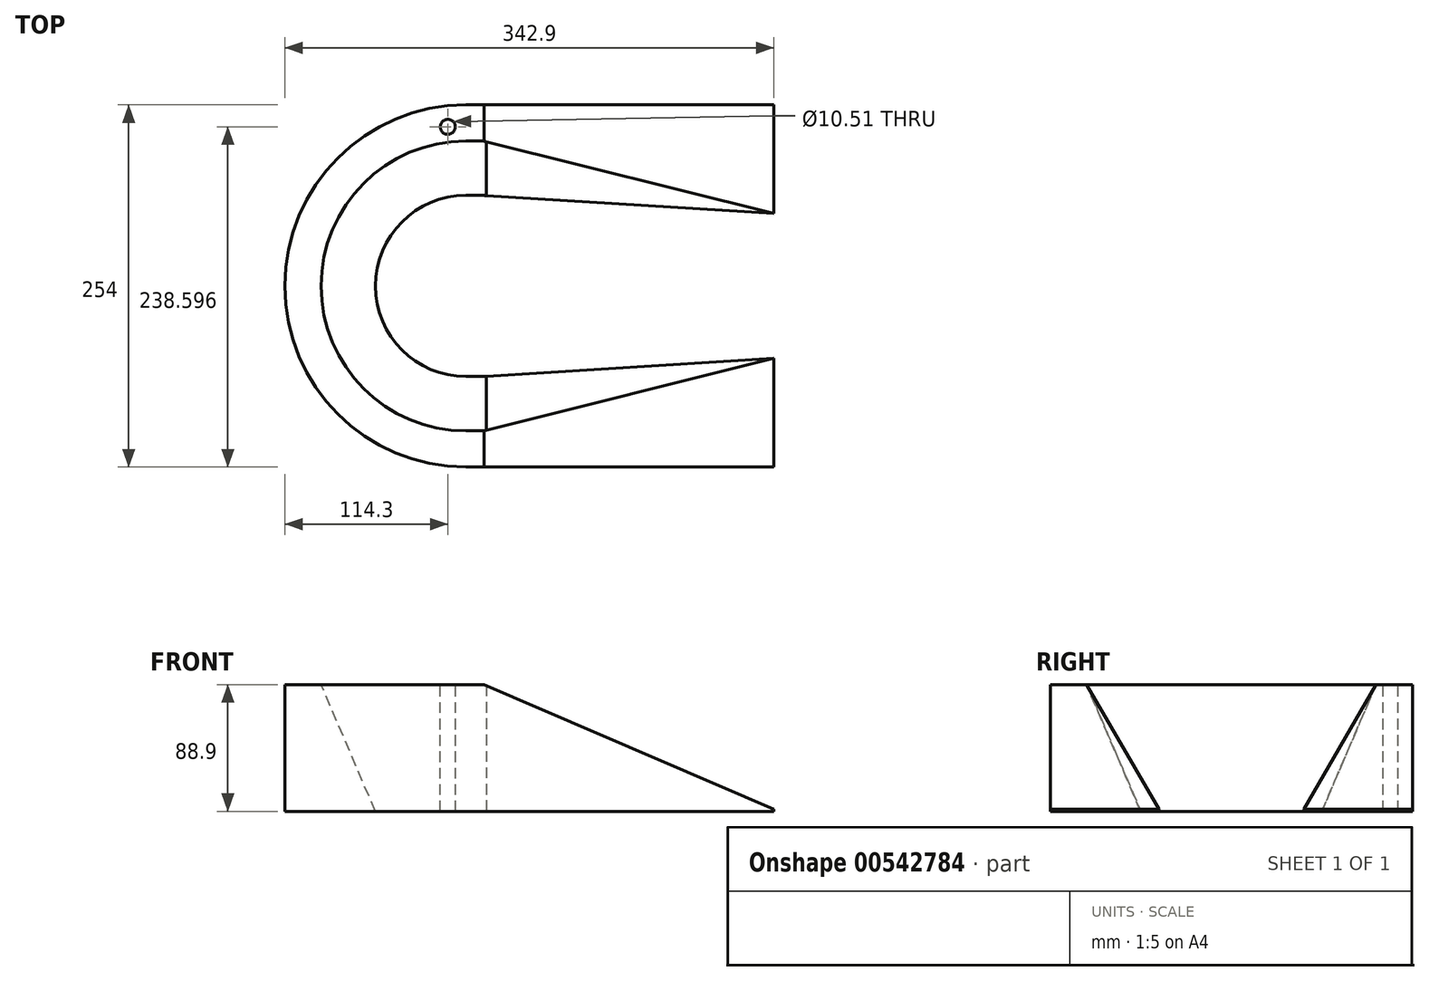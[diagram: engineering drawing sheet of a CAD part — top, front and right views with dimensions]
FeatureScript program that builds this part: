
annotation { "Feature Type Name" : "Feature", "Feature Type Description" : "" }
export const myFeature = defineFeature(function(context is Context, id is Id, definition is map)
    precondition{}
    {
        {
            var Q0;
            Q0=qCreatedBy(makeId("Top.planeOp"),FACE);
            var sketch = newSketch(context, id + "F0", { "sketchPlane" : qUnion([Q0])});
            skArc(sketch, "E0", {"start": v(0, 101.6) * mm, "mid": v(-71.84, 71.84) * mm, "end": v(-101.6, 0) * mm});
            skLineSegment(sketch, "E1", {"start": v(0, 101.6) * mm, "end": v(12.7, 101.6) * mm});
            skLineSegment(sketch, "E2", {"start": v(0, 0) * mm, "end": v(-101.6, 0) * mm, "construction": true});
            skSolve(sketch);
        }
        {
            var Q0;
            Q0=qCreatedBy(makeId("Right.planeOp"),FACE);
            var Q1;
            Q1=sQuery(id+"F0.wireOp",VERTEX,"E1.end");
            cPlane(context, id + "F1", {"entities" : qUnion([Q0, Q1]), "cplaneType" : CPlaneType.PLANE_POINT, "offset" : 25.4 * mm, "width" : 152.4 * mm, "height" : 152.4 * mm});
        }
        {
            var Q0;
            Q0=qCreatedBy(id+"F1.planeOp",FACE);
            var sketch = newSketch(context, id + "F2", { "sketchPlane" : qUnion([Q0])});
            skPoint(sketch, "E3.0", {"position": v(101.6, 0) * mm});
            skLineSegment(sketch, "E4", {"start": v(101.6, 0) * mm, "end": v(63.5, 0) * mm});
            skLineSegment(sketch, "E5", {"start": v(63.5, 0) * mm, "end": v(101.6, 88.9) * mm});
            skLineSegment(sketch, "E6", {"start": v(101.6, 88.9) * mm, "end": v(101.6, 0) * mm});
            skLineSegment(sketch, "E7", {"start": v(101.6, 88.9) * mm, "end": v(127, 88.9) * mm});
            skLineSegment(sketch, "E8", {"start": v(127, 88.9) * mm, "end": v(127, 0) * mm});
            skLineSegment(sketch, "E9", {"start": v(127, 0) * mm, "end": v(101.6, 0) * mm});
            skSolve(sketch);
        }
        {
            var Q0;
            Q0=makeQuery(id+"F2.imprint","IMPRINT",FACE,{"disambiguationData":[TD([[makeQuery(id+"F2.imprint","IMPRINT",EDGE,{"derivedFrom":sQuery(id+"F2.wireOp",EDGE,"E4")}),-1.0]])]});
            var Q1;
            Q1=makeQuery(id+"F2.imprint","IMPRINT",FACE,{"disambiguationData":[TD([[makeQuery(id+"F2.imprint","IMPRINT",EDGE,{"derivedFrom":sQuery(id+"F2.wireOp",EDGE,"E6")}),1.0]])]});
            var Q2;
            Q2=sQuery(id+"F0.wireOp",EDGE,"E0");
            var Q3;
            Q3=sQuery(id+"F0.wireOp",EDGE,"E1");
            var Q4;
            Q4=sQuery(id+"F0.wireOp",EDGE,"lOtsbc5z-2eFQ-w830-FJkx-ljFMD5zp9CMU");
            sweep(context, id + "F3", {"profiles" : qUnion([Q0, Q1]), "path" : qUnion([Q2, Q3, Q4])});
        }
        {
            var Q0;
            Q0=makeQuery(id+"F3.opSweep","CAP_FACE",FACE,{"disambiguationData":[OSD([sQuery(id+"F0.wireOp",VERTEX,"E1.end"),sQuery(id+"F2.wireOp",EDGE,"E4"),sQuery(id+"F2.wireOp",EDGE,"E5"),sQuery(id+"F2.wireOp",EDGE,"E7"),sQuery(id+"F2.wireOp",EDGE,"E8"),sQuery(id+"F2.wireOp",EDGE,"E9")])],"isStart":true});
            cPlane(context, id + "F4", {"entities" : qUnion([Q0]), "cplaneType" : CPlaneType.OFFSET, "offset" : 203.2 * mm, "width" : 152.4 * mm, "height" : 152.4 * mm});
        }
        {
            var Q0;
            Q0=qCreatedBy(id+"F4.planeOp",FACE);
            var sketch = newSketch(context, id + "F5", { "sketchPlane" : qUnion([Q0])});
            skLineSegment(sketch, "E10.top", {"start": v(50.8, 1.59) * mm, "end": v(127, 1.59) * mm});
            skLineSegment(sketch, "E10.right", {"start": v(127, 0) * mm, "end": v(127, 1.59) * mm});
            skLineSegment(sketch, "E11", {"start": v(50.8, 0) * mm, "end": v(127, 0) * mm});
            skLineSegment(sketch, "E12", {"start": v(50.8, 0) * mm, "end": v(50.8, 1.59) * mm});
            skSolve(sketch);
        }
        {
            var Q1;
            Q1=makeQuery(id+"F5.imprint","IMPRINT",FACE,{"disambiguationData":[TD([[makeQuery(id+"F5.imprint","IMPRINT",EDGE,{"derivedFrom":sQuery(id+"F5.wireOp",EDGE,"E10.top")}),-1.0]])]});
            var Q2;
            Q2=makeQuery(id+"F3.opSweep","CAP_FACE",FACE,{"disambiguationData":[OSD([sQuery(id+"F0.wireOp",VERTEX,"E1.end"),sQuery(id+"F2.wireOp",EDGE,"E4"),sQuery(id+"F2.wireOp",EDGE,"E5"),sQuery(id+"F2.wireOp",EDGE,"E7"),sQuery(id+"F2.wireOp",EDGE,"E8"),sQuery(id+"F2.wireOp",EDGE,"E9")])],"isStart":true});
            loft(context, id + "F6", {"operationType" : NewBodyOperationType.ADD, "sheetProfilesArray" : [{ "sheetProfileEntities" : qUnion([Q1]) }, { "sheetProfileEntities" : qUnion([Q2]) }]});
        }
        {
            var Q0;
            {var subQ0=sQuery(id+"F2.wireOp",EDGE,"E5");var subQ1=sQuery(id+"F0.wireOp",VERTEX,"E1.end");Q0=makeQuery(id+"F6.boolean.opBoolean","MERGE",EDGE,{"derivedFrom":[makeQuery(id+"F3.opSweep","CAP_EDGE",EDGE,{"disambiguationData":[OSD([subQ1,subQ0])],"isStart":true}),makeQuery(id+"F6.opLoft","MID_CAP_EDGE",EDGE,{"disambiguationData":[OSD([subQ1,sQuery(id+"F0.wireOp",EDGE,"E1"),sQuery(id+"F2.wireOp",EDGE,"E4"),subQ0,sQuery(id+"F2.wireOp",EDGE,"E6"),sQuery(id+"F2.wireOp",EDGE,"E7")])],"capPos":0.0})]});}
            var Q1;
            Q1=makeQuery(id+"F3.opSweep","MID_CAP_EDGE",EDGE,{"disambiguationData":[OSD([sQuery(id+"F0.wireOp",VERTEX,"E1.start"),sQuery(id+"F2.wireOp",EDGE,"E5")])],"capPos":1.0});
            fillet(context, id + "F7", {"entities" : qUnion([Q0, Q1]), "radius" : 50.8 * mm, "tangentPropagation" : true, "allowEdgeOverflow" : false});
        }
        {
            var Q0;
            Q0=makeQuery(id+"F3.opSweep","SWEPT_BODY",BODY,{"disambiguationData":[OSD([sQuery(id+"F0.wireOp",EDGE,"E1"),sQuery(id+"F2.wireOp",EDGE,"E4"),sQuery(id+"F2.wireOp",EDGE,"E5"),sQuery(id+"F2.wireOp",EDGE,"E7"),sQuery(id+"F2.wireOp",EDGE,"E8"),sQuery(id+"F2.wireOp",EDGE,"E9")])]});
            var Q1;
            Q1=makeQuery(id+"Fef9FZMCVwQ6fl1_1.boolean.opBoolean","MERGE",FACE,{"derivedFrom":[makeQuery(id+"F3.opSweep","CAP_FACE",FACE,{"disambiguationData":[OSD([sQuery(id+"F0.wireOp",VERTEX,"E0.end"),sQuery(id+"F2.wireOp",EDGE,"E4"),sQuery(id+"F2.wireOp",EDGE,"E5"),sQuery(id+"F2.wireOp",EDGE,"E7"),sQuery(id+"F2.wireOp",EDGE,"E8"),sQuery(id+"F2.wireOp",EDGE,"E9")])],"isStart":false}),makeQuery(id+"Fef9FZMCVwQ6fl1_1.opExtrude","SWEPT_FACE",FACE,{"disambiguationData":[OSD([sQuery(id+"Fh2OSJTHrX9CmkG_1.wireOp",EDGE,"yZ0BzBip-7MRC-nA9o-iIRe-HcukKyI0o2Tc.bottom")])]})]});
            mirror(context, id + "F8", {"operationType" : NewBodyOperationType.ADD, "entities" : qUnion([Q0]), "mirrorPlane" : qUnion([Q1])});
        }
        {
            var Q0;
            {var subQ0=makeQuery(id+"F3.opSweep","SWEPT_FACE",FACE,{"disambiguationData":[OSD([sQuery(id+"F0.wireOp",EDGE,"E1"),sQuery(id+"F2.wireOp",EDGE,"E7")])]});Q0=makeQuery(id+"F8.boolean.opBoolean","MERGE",FACE,{"derivedFrom":[subQ0,makeQuery(id+"F8.opPattern","COPY",FACE,{"derivedFrom":subQ0,"instanceName":"1"})]});}
            var sketch = newSketch(context, id + "F9", { "sketchPlane" : qUnion([Q0])});
            skPoint(sketch, "E13", {"position": v(-33.6, 106.78) * mm});
            skSolve(sketch);
        }
        {
            var Q0;
            {var subQ0=sQuery(id+"F2.wireOp",EDGE,"E8");var subQ1=sQuery(id+"F2.wireOp",EDGE,"E7");var subQ4=sQuery(id+"F0.wireOp",EDGE,"E1");var subQ9=makeQuery(id+"F3.opSweep","SWEPT_EDGE",EDGE,{"disambiguationData":[OSD([subQ4,subQ1,subQ0])]});Q0=makeQuery(id+"F9.imprint","IMPRINT",FACE,{"disambiguationData":[TD([[makeQuery(id+"F9.imprint","IMPRINT",EDGE,{"derivedFrom":subQ9}),1.0]])]});}
            var sketch = newSketch(context, id + "F10", { "sketchPlane" : qUnion([Q0])});
            skCircle(sketch, "E14", {"center": v(-12.7, 111.6) * mm, "radius": 5.26 * mm});
            skSolve(sketch);
        }
        {
            var Q0;
            Q0 = qSketchRegion(id + "F10", true);
            var sketch = newSketch(context, id + "F11", { "sketchPlane" : qUnion([Q0])});
            skSolve(sketch);
        }
        {
            var Q0;
            Q0 = qSketchRegion(id + "F11", true);
            var Q1;
            Q1=makeQuery(id+"F11.imprint","IMPRINT",FACE,{"disambiguationData":[TD([[makeQuery(id+"F11.imprint","IMPRINT",EDGE,{"derivedFrom":makeQuery(id+"F10.imprint","IMPRINT",EDGE,{"derivedFrom":sQuery(id+"F10.wireOp",EDGE,"E14")})}),1.0]])]});
            extrude(context, id + "F12", {"entities" : qUnion([Q0, Q1]), "operationType" : NewBodyOperationType.REMOVE, "endBound" : BoundingType.THROUGH_ALL, "oppositeDirection" : true, "depth" : 25.4 * mm, "offsetDistance" : 25.4 * mm});
        }
    });
